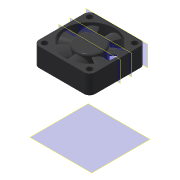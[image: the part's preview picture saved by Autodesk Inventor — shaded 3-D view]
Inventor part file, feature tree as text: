
AUTODESK INVENTOR PART (.ipt)
format: ipt  version: 2016 (Build 200138000, 138)  size: 329,728 bytes
history: native  units: mm
features: sketch x7, extrude x5, plane x3, fillet x2, pattern_circular x2, loft x1
ambient origin geometry x8: Origin, YZ Plane, XZ Plane, XY Plane, X Axis, Y Axis, Z Axis, Center Point
bodies: Solid1 (feature_tree), Solid2 (feature_tree)
feature tree (20):
  extrude  "Extrusion1"  Depth=10.0mm
  plane  "Work Plane1"
  fillet  "Fillet1"  Radius=10.0mm
  extrude  "Extrusion3"  Depth=3.0mm
  extrude  "Extrusion4"  Depth=3.0mm
  extrude  "Extrusion5"  Depth=100.0mm TaperAngle=0.0deg
  pattern_circular  "Circular Pattern1"  Count=3 Angle=360.0deg
  fillet  "Fillet2"  Radius=1.0mm
  plane  "Work Plane2"
  sketch  "Sketch6"  dims[d13=15.0mm]
  plane  "Work Plane3"
  loft  "Loft1"
  extrude  "Extrusion6"  Depth=10.0mm
  pattern_circular  "Circular Pattern2"  Angle=90.0deg  [1 undecoded]
  sketch  "Sketch1"  dims[d0=30.0mm d1=30.0mm d2=10.0mm d3=0.0mm]
  sketch  "Sketch3"  dims[d6=3.0mm d7=3.0mm]
  sketch  "Sketch4"  dims[d8=3.0mm d9=3.0mm]
  sketch  "Sketch5"  dims[d10=3.0mm d11=100.0mm d12=0.0mm]
  sketch  "Sketch7"  dims[d14=10.0mm d15=0.0mm]
  sketch  "Sketch8"  dims[d16=1.0mm d17=0.0mm d18=30.0mm d19=360.0deg d21=1.0mm d22=6.0mm d23=8.5mm d24=0.0mm d25=90.0deg d26=0.0mm d27=90.0deg d28=10.0mm d29=0.0mm d30=70.0mm d31=360.0deg]
note: 1 required parameter value undecoded (feature->parameter linkage not recoverable at this tier; creation-order binding heuristic only, values carry confidence <= 0.55)
